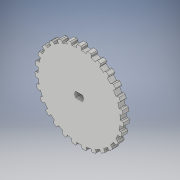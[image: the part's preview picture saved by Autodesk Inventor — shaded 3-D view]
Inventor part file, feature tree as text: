
AUTODESK INVENTOR PART (.ipt)
format: ipt  version: 2017 (Build 210142000, 142)  size: 392,192 bytes
history: native  units: in
note: dims shown in document units (in); Inventor stores cm internally (conversion verified against a paired STEP export)
features: extrude x3, sketch x3, pattern_circular x1
ambient origin geometry x8: Origin, YZ Plane, XZ Plane, XY Plane, X Axis, Y Axis, Z Axis, Center Point
bodies: Solid1 (feature_tree)
feature tree (7):
  extrude  "Extrusion1"  Depth=0.075in
  pattern_circular  "Circular Pattern1"  Count=108 Angle=360.0deg
  extrude  "Extrusion2"  Depth=0.062in
  extrude  "Extrusion3"  Depth=0.062in
  sketch  "Sketch1"  dims[d0=2.025in d4=0.075in]
  sketch  "Sketch2"  dims[d5=0.04in]
  sketch  "Sketch4"  dims[d6=0.04in d7=42.5197in d9=360.0deg d11=0.062in d12=0.062in d13=0.15in d14=0.0in d15=10.6299in d16=360.0deg d19=0.15in d20=0.0in d21=0.3862in d22=0.0in d23=0.133in d24=0.215in d25=0.0in]
